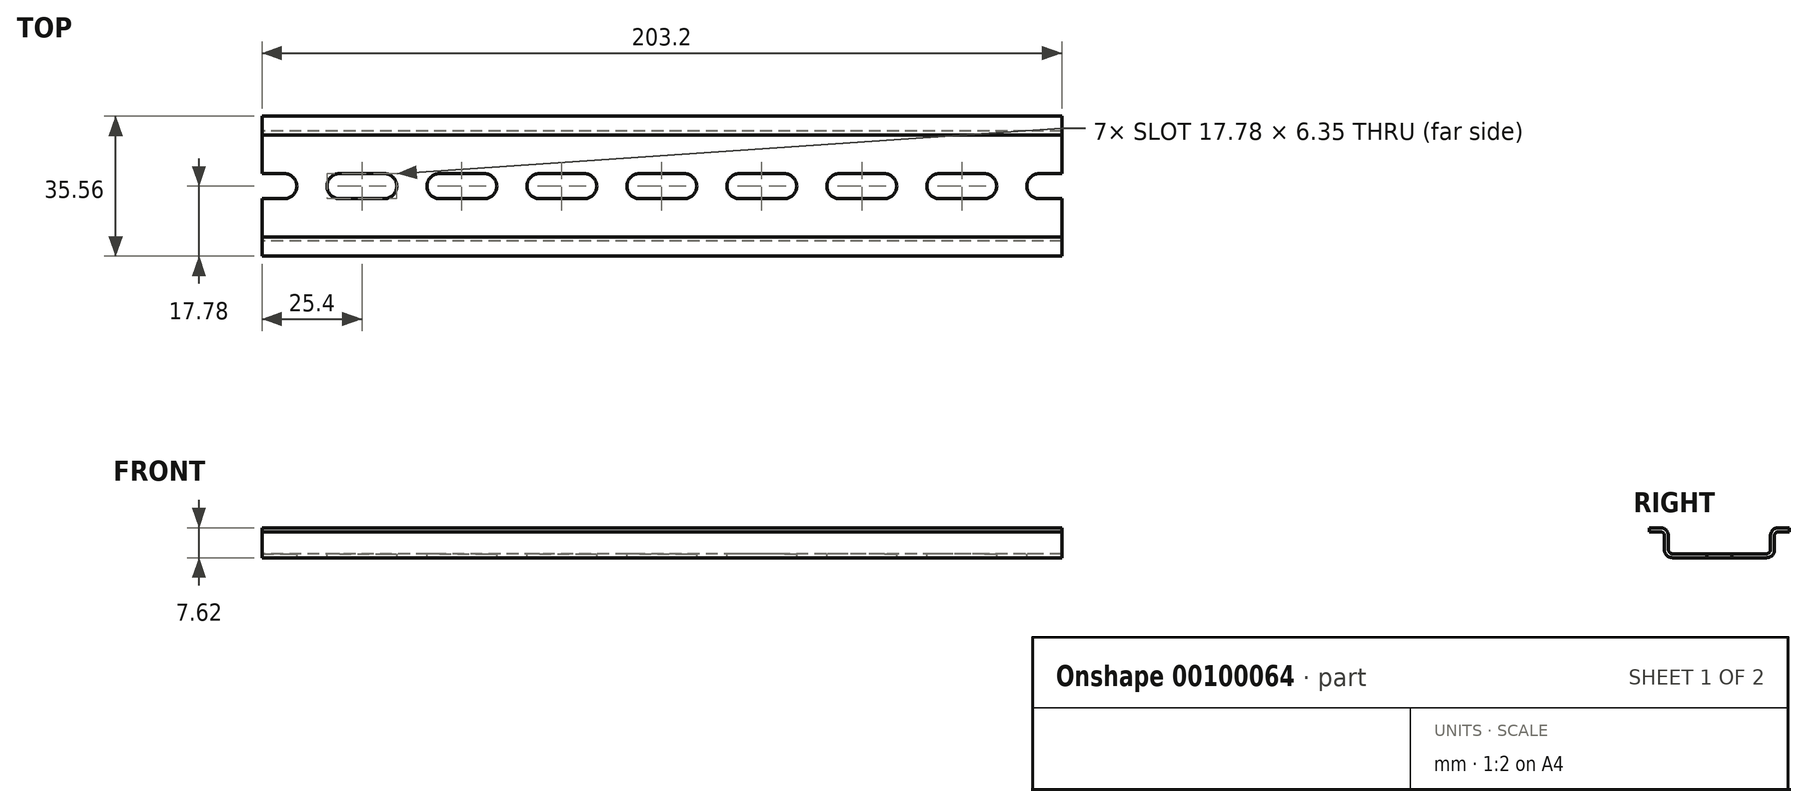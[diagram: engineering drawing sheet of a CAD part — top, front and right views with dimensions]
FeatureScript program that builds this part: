
annotation { "Feature Type Name" : "Feature", "Feature Type Description" : "" }
export const myFeature = defineFeature(function(context is Context, id is Id, definition is map)
    precondition{}
    {
        {
            var Q0;
            Q0=qCreatedBy(makeId("Right.planeOp"),FACE);
            var sketch = newSketch(context, id + "F0", { "sketchPlane" : qUnion([Q0])});
            skLineSegment(sketch, "E0", {"start": v(-13.98, -5.59) * mm, "end": v(-13.98, -2.03) * mm});
            skLineSegment(sketch, "E1", {"start": v(-15, -1.02) * mm, "end": v(-17.78, -1.02) * mm});
            skLineSegment(sketch, "E2", {"start": v(-17.78, -1.02) * mm, "end": v(-17.78, 0) * mm});
            skLineSegment(sketch, "E3", {"start": v(-17.78, 0) * mm, "end": v(-15, 0) * mm});
            skLineSegment(sketch, "E4", {"start": v(-12.96, -2.03) * mm, "end": v(-12.96, -5.59) * mm});
            skLineSegment(sketch, "E5", {"start": v(-11.95, -6.6) * mm, "end": v(11.95, -6.6) * mm});
            skLineSegment(sketch, "E6", {"start": v(12.96, -5.59) * mm, "end": v(12.96, -2.03) * mm});
            skLineSegment(sketch, "E7", {"start": v(15, 0) * mm, "end": v(17.78, 0) * mm});
            skLineSegment(sketch, "E8", {"start": v(17.78, 0) * mm, "end": v(17.78, -1.02) * mm});
            skLineSegment(sketch, "E9", {"start": v(17.78, -1.02) * mm, "end": v(15, -1.02) * mm});
            skLineSegment(sketch, "E10", {"start": v(13.98, -2.03) * mm, "end": v(13.98, -5.59) * mm});
            skLineSegment(sketch, "E11", {"start": v(11.95, -7.62) * mm, "end": v(-11.95, -7.62) * mm});
            skArc(sketch, "E12", {"start": v(-15, 0) * mm, "mid": v(-13.56, -0.6) * mm, "end": v(-12.96, -2.03) * mm});
            skArc(sketch, "E13", {"start": v(-13.98, -2.03) * mm, "mid": v(-14.28, -1.31) * mm, "end": v(-15, -1.02) * mm});
            skArc(sketch, "E14", {"start": v(-12.96, -5.59) * mm, "mid": v(-12.67, -6.3) * mm, "end": v(-11.95, -6.6) * mm});
            skArc(sketch, "E15", {"start": v(-11.95, -7.62) * mm, "mid": v(-13.38, -7.02) * mm, "end": v(-13.98, -5.59) * mm});
            skArc(sketch, "E16", {"start": v(11.95, -7.62) * mm, "mid": v(13.38, -7.02) * mm, "end": v(13.98, -5.59) * mm});
            skArc(sketch, "E17", {"start": v(11.95, -6.6) * mm, "mid": v(12.67, -6.3) * mm, "end": v(12.96, -5.59) * mm});
            skArc(sketch, "E18", {"start": v(13.98, -2.03) * mm, "mid": v(14.28, -1.31) * mm, "end": v(15, -1.02) * mm});
            skArc(sketch, "E19", {"start": v(12.96, -2.03) * mm, "mid": v(13.56, -0.6) * mm, "end": v(15, 0) * mm});
            skLineSegment(sketch, "E20", {"start": v(0, 0) * mm, "end": v(0, -6.6) * mm, "construction": true});
            skSolve(sketch);
        }
        {
            var Q0;
            Q0 = qSketchRegion(id + "F0", true);
            var Q1;
            Q1 = qConstructionFilter(qBodyType(qCreatedBy(id + "F0" ,EDGE), BodyType.WIRE), ConstructionObject.NO);
            extrude(context, id + "F1", {"entities" : qUnion([Q0]), "surfaceEntities" : qUnion([Q1]), "depth" : 203.2 * mm, "symmetric" : true});
        }
        {
            var Q0;
            Q0=makeQuery(id+"F1.opExtrude","SWEPT_FACE",FACE,{"disambiguationData":[OSD([sQuery(id+"F0.wireOp",EDGE,"E5")])]});
            var sketch = newSketch(context, id + "F2", { "sketchPlane" : qUnion([Q0])});
            skArc(sketch, "E21", {"start": v(5.72, -3.17) * mm, "mid": v(8.9, 0) * mm, "end": v(5.71, 3.18) * mm});
            skArc(sketch, "E22", {"start": v(-5.72, 3.17) * mm, "mid": v(-8.89, 0) * mm, "end": v(-5.71, -3.17) * mm});
            skLineSegment(sketch, "E23", {"start": v(-5.72, 3.18) * mm, "end": v(5.71, 3.18) * mm});
            skLineSegment(sketch, "E24", {"start": v(5.72, -3.17) * mm, "end": v(-5.71, -3.17) * mm});
            skLineSegment(sketch, "E25", {"start": v(-5.72, 0) * mm, "end": v(0, 0) * mm, "construction": true});
            skLineSegment(sketch, "E26", {"start": v(0, 0) * mm, "end": v(5.72, 0) * mm, "construction": true});
            skLineSegment(sketch, "E27.1.0.0", {"start": v(19.68, 0) * mm, "end": v(25.4, 0) * mm, "construction": true});
            skArc(sketch, "E27.1.0.1", {"start": v(31.12, -3.17) * mm, "mid": v(34.3, 0) * mm, "end": v(31.12, 3.18) * mm});
            skArc(sketch, "E27.1.0.2", {"start": v(19.68, 3.17) * mm, "mid": v(16.51, 0) * mm, "end": v(19.68, -3.17) * mm});
            skLineSegment(sketch, "E27.1.0.3", {"start": v(25.4, 0) * mm, "end": v(31.11, 0) * mm, "construction": true});
            skLineSegment(sketch, "E27.1.0.4", {"start": v(31.11, -3.17) * mm, "end": v(19.68, -3.17) * mm});
            skLineSegment(sketch, "E27.1.0.5", {"start": v(19.69, 3.18) * mm, "end": v(31.12, 3.18) * mm});
            skLineSegment(sketch, "E27.2.0.0", {"start": v(45.08, 0) * mm, "end": v(50.8, 0) * mm, "construction": true});
            skArc(sketch, "E27.2.0.1", {"start": v(56.51, -3.17) * mm, "mid": v(59.69, 0) * mm, "end": v(56.51, 3.18) * mm});
            skArc(sketch, "E27.2.0.2", {"start": v(45.09, 3.17) * mm, "mid": v(41.91, 0) * mm, "end": v(45.09, -3.17) * mm});
            skLineSegment(sketch, "E27.2.0.3", {"start": v(50.8, 0) * mm, "end": v(56.52, 0) * mm, "construction": true});
            skLineSegment(sketch, "E27.2.0.4", {"start": v(56.51, -3.17) * mm, "end": v(45.09, -3.17) * mm});
            skLineSegment(sketch, "E27.2.0.5", {"start": v(45.09, 3.18) * mm, "end": v(56.51, 3.18) * mm});
            skLineSegment(sketch, "E27.3.0.0", {"start": v(70.48, 0) * mm, "end": v(76.2, 0) * mm, "construction": true});
            skArc(sketch, "E27.3.0.1", {"start": v(81.91, -3.17) * mm, "mid": v(85.09, 0) * mm, "end": v(81.91, 3.18) * mm});
            skArc(sketch, "E27.3.0.2", {"start": v(70.48, 3.17) * mm, "mid": v(67.3, 0) * mm, "end": v(70.48, -3.17) * mm});
            skLineSegment(sketch, "E27.3.0.3", {"start": v(76.2, 0) * mm, "end": v(81.91, 0) * mm, "construction": true});
            skLineSegment(sketch, "E27.3.0.4", {"start": v(81.92, -3.17) * mm, "end": v(70.48, -3.17) * mm});
            skLineSegment(sketch, "E27.3.0.5", {"start": v(70.48, 3.18) * mm, "end": v(81.91, 3.18) * mm});
            skLineSegment(sketch, "E27.4.0.0", {"start": v(95.88, 0) * mm, "end": v(101.6, 0) * mm, "construction": true});
            skArc(sketch, "E27.4.0.1", {"start": v(107.31, -3.17) * mm, "mid": v(110.49, 0) * mm, "end": v(107.31, 3.18) * mm});
            skArc(sketch, "E27.4.0.2", {"start": v(95.88, 3.17) * mm, "mid": v(92.7, 0) * mm, "end": v(95.88, -3.17) * mm});
            skLineSegment(sketch, "E27.4.0.3", {"start": v(101.6, 0) * mm, "end": v(107.31, 0) * mm, "construction": true});
            skLineSegment(sketch, "E27.4.0.4", {"start": v(107.32, -3.17) * mm, "end": v(95.88, -3.17) * mm});
            skLineSegment(sketch, "E27.4.0.5", {"start": v(95.88, 3.18) * mm, "end": v(107.31, 3.18) * mm});
            skLineSegment(sketch, "E27.direction1", {"start": v(-5.71, -3.17) * mm, "end": v(19.69, -3.17) * mm, "construction": true});
            skLineSegment(sketch, "E28.1.0.0", {"start": v(-25.4, 0) * mm, "end": v(-19.69, 0) * mm, "construction": true});
            skLineSegment(sketch, "E28.1.0.1", {"start": v(-31.12, 0) * mm, "end": v(-25.4, 0) * mm, "construction": true});
            skLineSegment(sketch, "E28.1.0.2", {"start": v(-31.12, 3.18) * mm, "end": v(-19.69, 3.18) * mm});
            skArc(sketch, "E28.1.0.3", {"start": v(-31.12, 3.17) * mm, "mid": v(-34.3, 0) * mm, "end": v(-31.12, -3.17) * mm});
            skArc(sketch, "E28.1.0.4", {"start": v(-19.69, -3.17) * mm, "mid": v(-16.51, 0) * mm, "end": v(-19.69, 3.18) * mm});
            skLineSegment(sketch, "E28.1.0.5", {"start": v(-19.69, -3.17) * mm, "end": v(-31.12, -3.17) * mm});
            skLineSegment(sketch, "E28.2.0.0", {"start": v(-50.8, 0) * mm, "end": v(-45.09, 0) * mm, "construction": true});
            skLineSegment(sketch, "E28.2.0.1", {"start": v(-56.52, 0) * mm, "end": v(-50.8, 0) * mm, "construction": true});
            skLineSegment(sketch, "E28.2.0.2", {"start": v(-56.52, 3.18) * mm, "end": v(-45.09, 3.18) * mm});
            skArc(sketch, "E28.2.0.3", {"start": v(-56.52, 3.17) * mm, "mid": v(-59.7, 0) * mm, "end": v(-56.52, -3.17) * mm});
            skArc(sketch, "E28.2.0.4", {"start": v(-45.09, -3.17) * mm, "mid": v(-41.91, 0) * mm, "end": v(-45.09, 3.18) * mm});
            skLineSegment(sketch, "E28.2.0.5", {"start": v(-45.09, -3.17) * mm, "end": v(-56.52, -3.17) * mm});
            skLineSegment(sketch, "E28.3.0.0", {"start": v(-76.2, 0) * mm, "end": v(-70.49, 0) * mm, "construction": true});
            skLineSegment(sketch, "E28.3.0.1", {"start": v(-81.92, 0) * mm, "end": v(-76.2, 0) * mm, "construction": true});
            skLineSegment(sketch, "E28.3.0.2", {"start": v(-81.92, 3.18) * mm, "end": v(-70.49, 3.18) * mm});
            skArc(sketch, "E28.3.0.3", {"start": v(-81.92, 3.17) * mm, "mid": v(-85.1, 0) * mm, "end": v(-81.92, -3.17) * mm});
            skArc(sketch, "E28.3.0.4", {"start": v(-70.49, -3.17) * mm, "mid": v(-67.31, 0) * mm, "end": v(-70.49, 3.18) * mm});
            skLineSegment(sketch, "E28.3.0.5", {"start": v(-70.48, -3.17) * mm, "end": v(-81.92, -3.17) * mm});
            skLineSegment(sketch, "E28.4.0.0", {"start": v(-101.6, 0) * mm, "end": v(-95.89, 0) * mm, "construction": true});
            skLineSegment(sketch, "E28.4.0.1", {"start": v(-107.32, 0) * mm, "end": v(-101.6, 0) * mm, "construction": true});
            skLineSegment(sketch, "E28.4.0.2", {"start": v(-107.32, 3.18) * mm, "end": v(-95.89, 3.18) * mm});
            skArc(sketch, "E28.4.0.3", {"start": v(-107.32, 3.17) * mm, "mid": v(-110.5, 0) * mm, "end": v(-107.32, -3.17) * mm});
            skArc(sketch, "E28.4.0.4", {"start": v(-95.89, -3.17) * mm, "mid": v(-92.71, 0) * mm, "end": v(-95.89, 3.18) * mm});
            skLineSegment(sketch, "E28.4.0.5", {"start": v(-95.89, -3.17) * mm, "end": v(-107.32, -3.17) * mm});
            skLineSegment(sketch, "E28.direction1", {"start": v(-5.71, -3.17) * mm, "end": v(-31.12, -3.17) * mm, "construction": true});
            skSolve(sketch);
        }
        {
            var Q0;
            Q0 = qSketchRegion(id + "F2", true);
            extrude(context, id + "F3", {"entities" : qUnion([Q0]), "operationType" : NewBodyOperationType.REMOVE, "endBound" : BoundingType.THROUGH_ALL, "oppositeDirection" : true, "depth" : 25.4 * mm});
        }
    });
